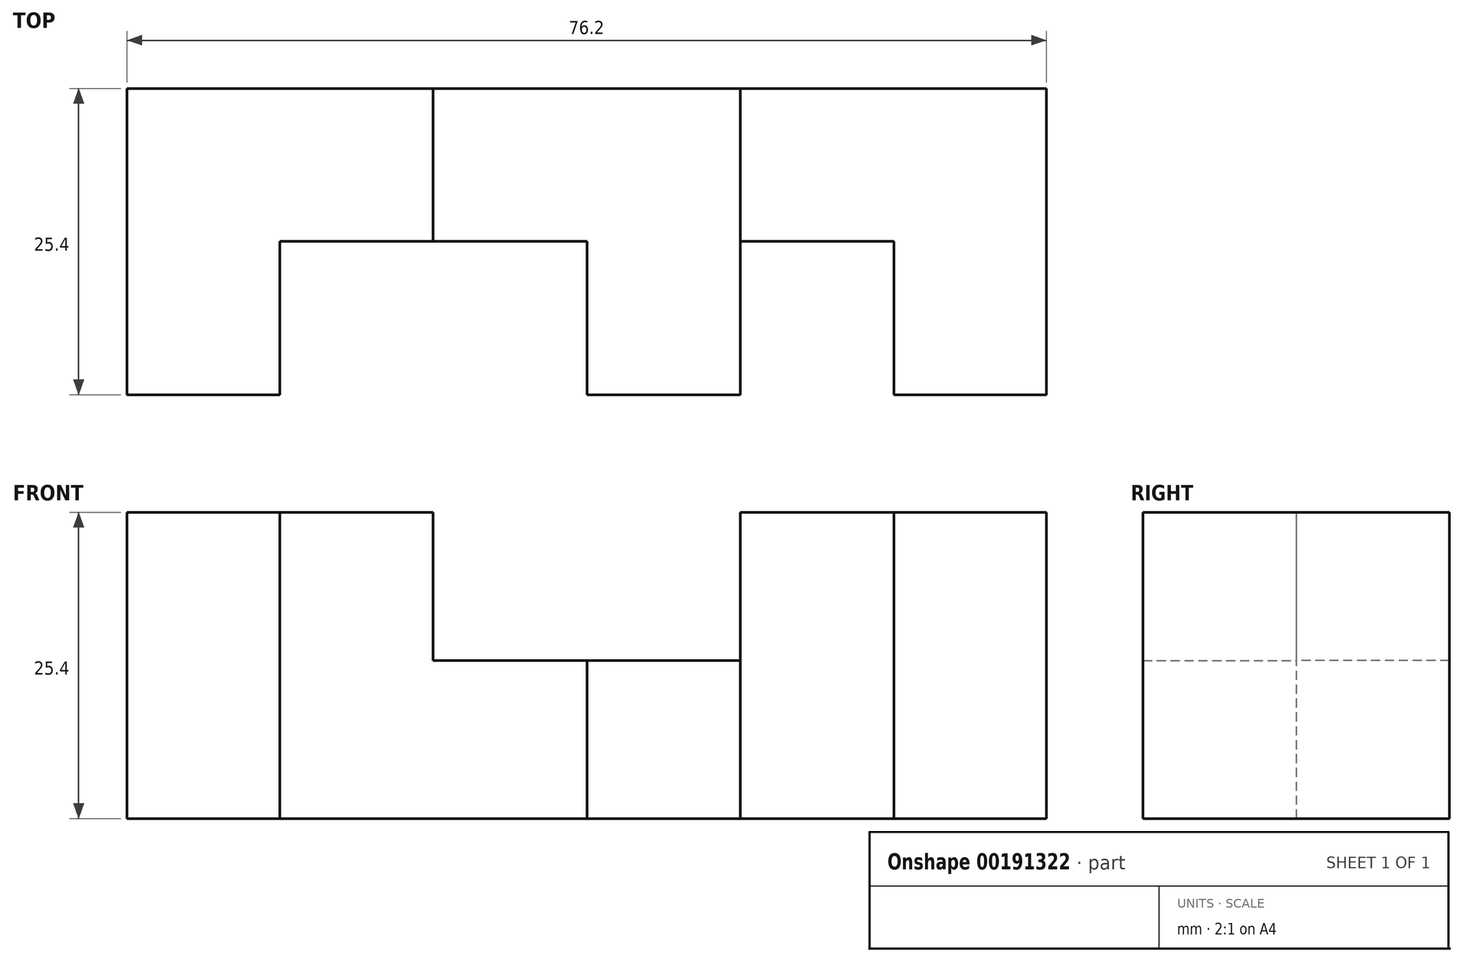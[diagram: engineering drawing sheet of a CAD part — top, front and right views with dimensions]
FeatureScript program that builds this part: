
annotation { "Feature Type Name" : "Feature", "Feature Type Description" : "" }
export const myFeature = defineFeature(function(context is Context, id is Id, definition is map)
    precondition{}
    {
        {
            var Q0;
            Q0=qCreatedBy(makeId("Top.planeOp"),FACE);
            var sketch = newSketch(context, id + "F0", { "sketchPlane" : qUnion([Q0])});
            skLineSegment(sketch, "E0.bottom", {"start": v(0, 0) * mm, "end": v(76.2, 0) * mm});
            skLineSegment(sketch, "E0.top", {"start": v(0, 25.4) * mm, "end": v(76.2, 25.4) * mm});
            skLineSegment(sketch, "E0.left", {"start": v(0, 0) * mm, "end": v(0, 25.4) * mm});
            skLineSegment(sketch, "E0.right", {"start": v(76.2, 0) * mm, "end": v(76.2, 25.4) * mm});
            skSolve(sketch);
        }
        {
            var Q0;
            Q0=makeQuery(id+"F0.imprint","IMPRINT",FACE,{"disambiguationData":[TD([[makeQuery(id+"F0.imprint","IMPRINT",EDGE,{"derivedFrom":sQuery(id+"F0.wireOp",EDGE,"E0.bottom")}),1.0]])]});
            extrude(context, id + "F1", {"entities" : qUnion([Q0]), "depth" : 25.4 * mm});
        }
        {
            var Q0;
            Q0=qCreatedBy(makeId("Front.planeOp"),FACE);
            var sketch = newSketch(context, id + "F2", { "sketchPlane" : qUnion([Q0])});
            skLineSegment(sketch, "E1.bottom", {"start": v(25.37, 25.82) * mm, "end": v(50.83, 25.82) * mm});
            skLineSegment(sketch, "E1.top", {"start": v(25.37, 13.1) * mm, "end": v(50.83, 13.1) * mm});
            skLineSegment(sketch, "E1.left", {"start": v(25.37, 25.82) * mm, "end": v(25.37, 13.1) * mm});
            skLineSegment(sketch, "E1.right", {"start": v(50.83, 25.82) * mm, "end": v(50.83, 13.1) * mm});
            skSolve(sketch);
        }
        {
            var Q0;
            Q0=makeQuery(id+"F2.imprint","IMPRINT",FACE,{"disambiguationData":[TD([[makeQuery(id+"F2.imprint","IMPRINT",EDGE,{"derivedFrom":sQuery(id+"F2.wireOp",EDGE,"E1.bottom")}),-1.0]])]});
            extrude(context, id + "F3", {"entities" : qUnion([Q0]), "operationType" : NewBodyOperationType.REMOVE, "oppositeDirection" : true, "depth" : 25.4 * mm});
        }
        {
            var Q0;
            {var subQ0=sQuery(id+"F0.wireOp",EDGE,"E0.bottom");var subQ1=sQuery(id+"F0.wireOp",EDGE,"E0.top");var subQ2=sQuery(id+"F0.wireOp",EDGE,"E0.right");Q0=makeQuery(id+"F3.boolean.opBoolean","SPLIT",FACE,{"disambiguationData":[TD([makeQuery(id+"F1.opExtrude","SWEPT_FACE",FACE,{"disambiguationData":[OSD([subQ2])]})])],"derivedFrom":makeQuery(id+"F1.opExtrude","CAP_FACE",FACE,{"disambiguationData":[OSD([subQ0,subQ1,sQuery(id+"F0.wireOp",EDGE,"E0.left"),subQ2])],"isStart":false})});}
            var sketch = newSketch(context, id + "F4", { "sketchPlane" : qUnion([Q0])});
            skLineSegment(sketch, "E2.bottom", {"start": v(50.83, 0) * mm, "end": v(63.55, 0) * mm});
            skLineSegment(sketch, "E2.top", {"start": v(50.83, 12.73) * mm, "end": v(63.55, 12.73) * mm});
            skLineSegment(sketch, "E2.left", {"start": v(50.83, 0) * mm, "end": v(50.83, 12.73) * mm});
            skLineSegment(sketch, "E2.right", {"start": v(63.55, 0) * mm, "end": v(63.55, 12.73) * mm});
            skSolve(sketch);
        }
        {
            var Q0;
            Q0=makeQuery(id+"F4.imprint","IMPRINT",FACE,{"disambiguationData":[TD([[makeQuery(id+"F4.imprint","IMPRINT",EDGE,{"derivedFrom":sQuery(id+"F4.wireOp",EDGE,"E2.bottom")}),1.0]])]});
            extrude(context, id + "F5", {"entities" : qUnion([Q0]), "operationType" : NewBodyOperationType.REMOVE, "oppositeDirection" : true, "depth" : 25.4 * mm});
        }
        {
            var Q0;
            Q0=qCreatedBy(makeId("Top.planeOp"),FACE);
            var sketch = newSketch(context, id + "F6", { "sketchPlane" : qUnion([Q0])});
            skLineSegment(sketch, "E3.bottom", {"start": v(12.67, 0) * mm, "end": v(38.13, 0) * mm});
            skLineSegment(sketch, "E3.top", {"start": v(12.67, 12.73) * mm, "end": v(38.13, 12.73) * mm});
            skLineSegment(sketch, "E3.left", {"start": v(12.67, 0) * mm, "end": v(12.67, 12.73) * mm});
            skLineSegment(sketch, "E3.right", {"start": v(38.13, 0) * mm, "end": v(38.13, 12.73) * mm});
            skSolve(sketch);
        }
        {
            var Q0;
            Q0=makeQuery(id+"F6.imprint","IMPRINT",FACE,{"disambiguationData":[TD([[makeQuery(id+"F6.imprint","IMPRINT",EDGE,{"derivedFrom":sQuery(id+"F6.wireOp",EDGE,"E3.bottom")}),1.0]])]});
            extrude(context, id + "F7", {"entities" : qUnion([Q0]), "operationType" : NewBodyOperationType.REMOVE, "depth" : 25.65 * mm});
        }
    });
